# Revit family: 205_LRCA 1000
name_source: partatom
category: Duct Accessories
revit_build: Autodesk Revit 2018 (Build: 20170223_1515(x64)
units: mm (PartAtom-declared; Revit-internal decimal feet)

## family parameters
Always vertical = Yes
Cut with Voids When Loaded = No
Part Type = Breaks Into
Round Connector Dimension = Use Diameter
Shared = No
Work Plane-Based = No

## types (3) — shared parameters
CAT0 = Yes
Description = Silencer rectangular L=1000mm
H2D = 181 mm
L = 1000 mm  [stored 3.28084 ft]
L2D = 1000 mm  [stored 3.28084 ft]
LL = 500 mm  [stored 1.64042 ft]
Manufacturer = Flexit
QmdConnectorList = 201;D;202;D
URL = www.flexit.no
W2D = 239 mm
magiPartTypeId = 205
magiProductFamilyId = LRCA 1000

## per-type parameters (varying)
| type | CBB | CHH | D | magiProductId |
| 125-116750 | 120 mm | 91 mm | 125 mm | LRCA 125 1000 |
| 160-116751 | 138 mm | 109 mm | 160 mm | LRCA 160 1000 |
| 200-116752 | 164 mm  [stored 0.538058 ft] | 127 mm  [stored 0.416667 ft] | 200 mm | LRCA 200 1000 |

note: column(s) folded — value = type name in every type: MC Product Code

note: [stored X ft] marks values corroborated as IEEE doubles in the binary element streams (Revit-internal decimal feet)

## geometry (parser evidence)
native form markers: Sweep x2
no freeform markers — native parametric forms only
